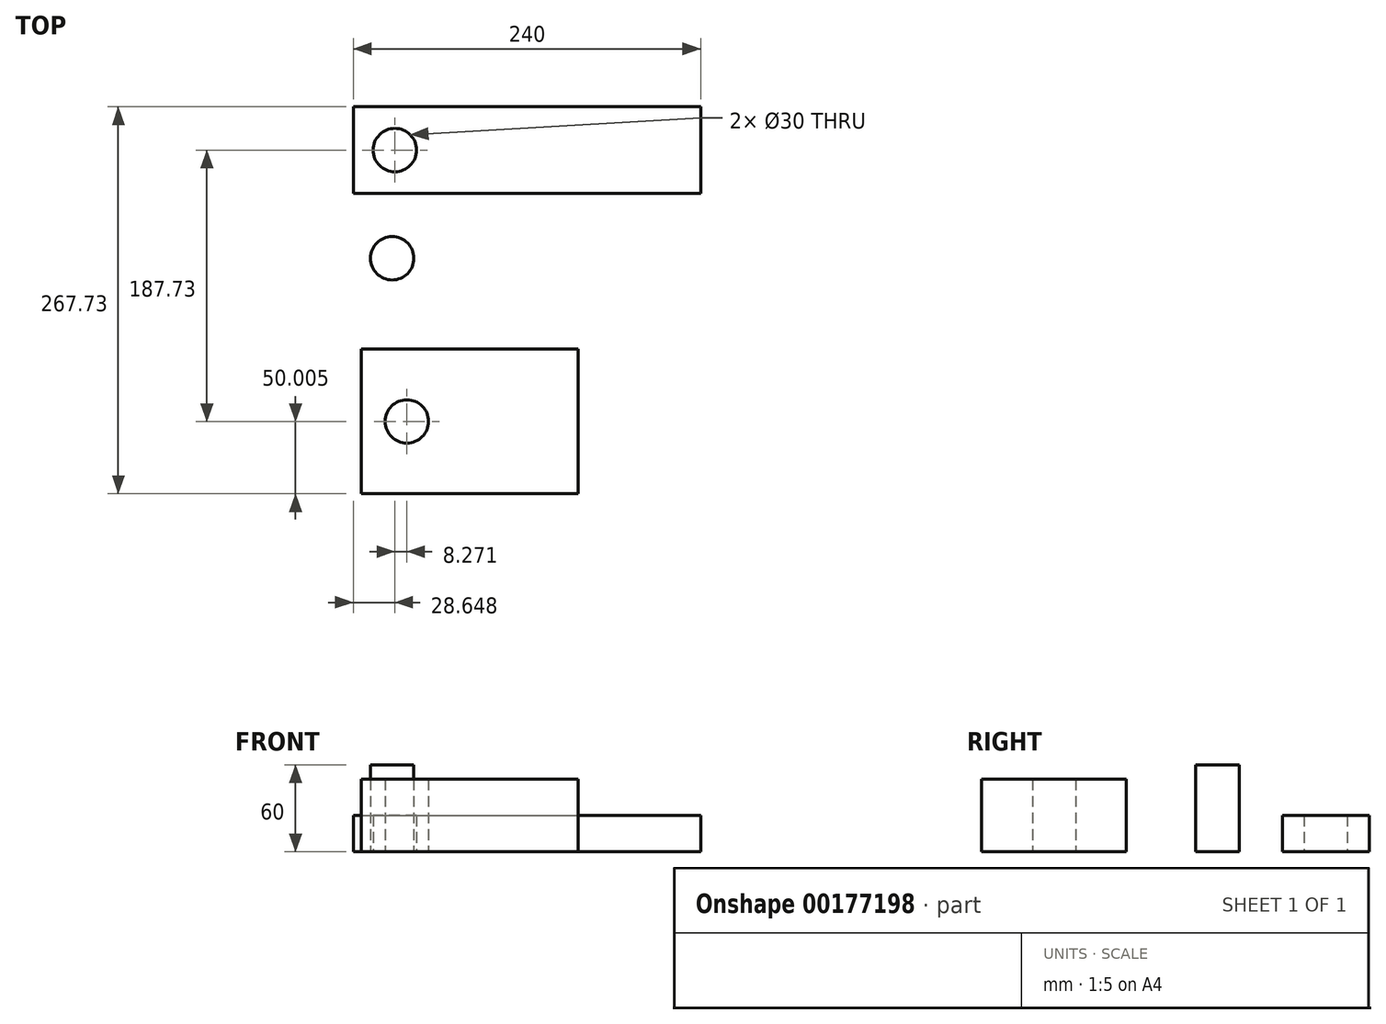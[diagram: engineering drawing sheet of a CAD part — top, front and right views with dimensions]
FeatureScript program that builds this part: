
annotation { "Feature Type Name" : "Feature", "Feature Type Description" : "" }
export const myFeature = defineFeature(function(context is Context, id is Id, definition is map)
    precondition{}
    {
        {
            var Q0;
            Q0=qCreatedBy(makeId("Top.planeOp"),FACE);
            var sketch = newSketch(context, id + "F0", { "sketchPlane" : qUnion([Q0])});
            skLineSegment(sketch, "E0.bottom", {"start": v(-61.53, 49.67) * mm, "end": v(178.47, 49.67) * mm});
            skLineSegment(sketch, "E0.top", {"start": v(-61.53, -10.33) * mm, "end": v(178.47, -10.33) * mm});
            skLineSegment(sketch, "E0.left", {"start": v(-61.53, 49.67) * mm, "end": v(-61.53, -10.33) * mm});
            skLineSegment(sketch, "E0.right", {"start": v(178.47, 49.67) * mm, "end": v(178.47, -10.33) * mm});
            skCircle(sketch, "E1", {"center": v(-32.88, 19.67) * mm, "radius": 15 * mm});
            skSolve(sketch);
        }
        {
            var Q0;
            Q0=makeQuery(id+"F0.imprint","IMPRINT",FACE,{"disambiguationData":[TD([[makeQuery(id+"F0.imprint","IMPRINT",EDGE,{"derivedFrom":sQuery(id+"F0.wireOp",EDGE,"E0.bottom")}),-1.0]])]});
            extrude(context, id + "F1", {"entities" : qUnion([Q0]), "depth" : 25 * mm});
        }
        {
            var Q0;
            Q0=qCreatedBy(makeId("Top.planeOp"),FACE);
            var sketch = newSketch(context, id + "F2", { "sketchPlane" : qUnion([Q0])});
            skCircle(sketch, "E2", {"center": v(-34.75, -55.14) * mm, "radius": 15 * mm});
            skSolve(sketch);
        }
        {
            var Q0;
            Q0=makeQuery(id+"F2.imprint","IMPRINT",FACE,{"disambiguationData":[TD([[makeQuery(id+"F2.imprint","IMPRINT",EDGE,{"derivedFrom":sQuery(id+"F2.wireOp",EDGE,"E2")}),1.0]])]});
            extrude(context, id + "F3", {"entities" : qUnion([Q0]), "depth" : 60 * mm});
        }
        {
            var Q0;
            Q0=qCreatedBy(makeId("Top.planeOp"),FACE);
            var sketch = newSketch(context, id + "F4", { "sketchPlane" : qUnion([Q0])});
            skLineSegment(sketch, "E3.bottom", {"start": v(-56.1, -118.06) * mm, "end": v(93.9, -118.06) * mm});
            skLineSegment(sketch, "E3.top", {"start": v(-56.1, -218.06) * mm, "end": v(93.9, -218.06) * mm});
            skLineSegment(sketch, "E3.left", {"start": v(-56.1, -118.06) * mm, "end": v(-56.1, -218.06) * mm});
            skLineSegment(sketch, "E3.right", {"start": v(93.9, -118.06) * mm, "end": v(93.9, -218.06) * mm});
            skCircle(sketch, "E4", {"center": v(-24.61, -168.06) * mm, "radius": 15 * mm});
            skSolve(sketch);
        }
        {
            var Q0;
            Q0=makeQuery(id+"F4.imprint","IMPRINT",FACE,{"disambiguationData":[TD([[makeQuery(id+"F4.imprint","IMPRINT",EDGE,{"derivedFrom":sQuery(id+"F4.wireOp",EDGE,"E3.bottom")}),-1.0]])]});
            extrude(context, id + "F5", {"entities" : qUnion([Q0]), "depth" : 50 * mm});
        }
    });
